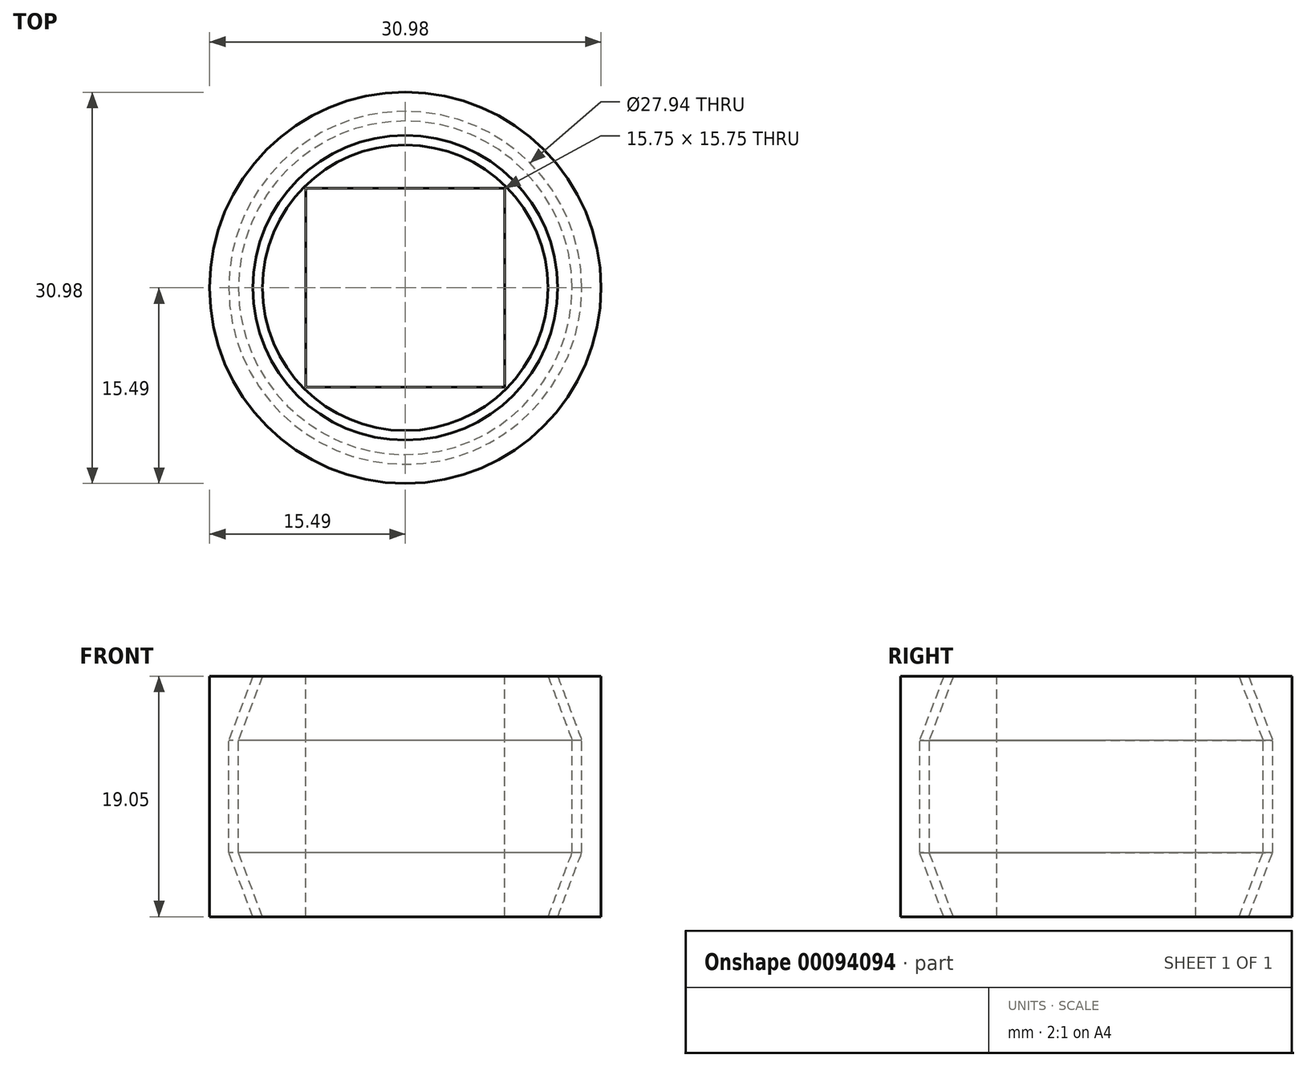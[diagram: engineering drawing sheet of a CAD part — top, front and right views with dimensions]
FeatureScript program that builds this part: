
annotation { "Feature Type Name" : "Feature", "Feature Type Description" : "" }
export const myFeature = defineFeature(function(context is Context, id is Id, definition is map)
    precondition{}
    {
        {
            var Q0;
            Q0=qCreatedBy(makeId("Front.planeOp"),FACE);
            var sketch = newSketch(context, id + "F0", { "sketchPlane" : qUnion([Q0])});
            skLineSegment(sketch, "E0", {"start": v(0, 52.04) * mm, "end": v(0, -73.81) * mm, "construction": true});
            skLineSegment(sketch, "E1.bottom", {"start": v(0, 19.05) * mm, "end": v(13.2, 19.05) * mm});
            skLineSegment(sketch, "E1.top", {"start": v(0, 0) * mm, "end": v(13.2, 0) * mm});
            skLineSegment(sketch, "E1.left", {"start": v(0, 19.05) * mm, "end": v(0, 0) * mm});
            skLineSegment(sketch, "E1.right", {"start": v(13.2, 19.05) * mm, "end": v(13.2, 0) * mm});
            skSolve(sketch);
        }
        {
            var Q0;
            Q0=makeQuery(id+"F0.imprint","IMPRINT",FACE,{"disambiguationData":[TD([[makeQuery(id+"F0.imprint","IMPRINT",EDGE,{"derivedFrom":sQuery(id+"F0.wireOp",EDGE,"E1.bottom")}),-1.0]])]});
            var Q1;
            Q1=sQuery(id+"F0.wireOp",EDGE,"E0");
            revolve(context, id + "F1", {"entities" : qUnion([Q0]), "axis" : qUnion([Q1]), "revolveType" : RevolveType.FULL});
        }
        {
            var Q0;
            Q0=makeQuery(id+"F1.opRevolve","SWEPT_FACE",FACE,{"disambiguationData":[OSD([sQuery(id+"F0.wireOp",EDGE,"E1.bottom")])]});
            var sketch = newSketch(context, id + "F2", { "sketchPlane" : qUnion([Q0])});
            skLineSegment(sketch, "E2.bottom", {"start": v(-7.87, 7.87) * mm, "end": v(7.87, 7.87) * mm});
            skLineSegment(sketch, "E2.top", {"start": v(-7.87, -7.87) * mm, "end": v(7.87, -7.87) * mm});
            skLineSegment(sketch, "E2.left", {"start": v(-7.87, 7.87) * mm, "end": v(-7.87, -7.87) * mm});
            skLineSegment(sketch, "E2.right", {"start": v(7.87, 7.87) * mm, "end": v(7.87, -7.87) * mm});
            skLineSegment(sketch, "E3", {"start": v(-7.87, 0) * mm, "end": v(7.87, 0) * mm, "construction": true});
            skPoint(sketch, "E4", {"position": v(0, 0) * mm});
            skSolve(sketch);
        }
        {
            var Q0;
            {var subQ0=sQuery(id+"F2.wireOp",EDGE,"E2.left");var subQ1=sQuery(id+"F2.wireOp",EDGE,"E2.bottom");var subQ2=makeQuery(id+"F2.imprint","INTERSECT",VERTEX,{"derivedFrom":[subQ1,subQ0]});Q0=makeQuery(id+"F2.imprint","IMPRINT",FACE,{"disambiguationData":[TD([[makeQuery(id+"F2.imprint","IMPRINT",EDGE,{"disambiguationData":[TD([[subQ2,-1.0]])],"derivedFrom":subQ1}),-1.0]])]});}
            var Q1;
            {var subQ0=sQuery(id+"F2.wireOp",EDGE,"E2.right");var subQ1=sQuery(id+"F2.wireOp",EDGE,"E2.bottom");var subQ2=makeQuery(id+"F2.imprint","INTERSECT",VERTEX,{"derivedFrom":[subQ1,subQ0]});Q1=makeQuery(id+"F2.imprint","IMPRINT",FACE,{"disambiguationData":[TD([[makeQuery(id+"F2.imprint","IMPRINT",EDGE,{"disambiguationData":[TD([[subQ2,1.0]])],"derivedFrom":subQ1}),-1.0]])]});}
            var Q2;
            {var subQ0=sQuery(id+"F2.wireOp",EDGE,"E2.left");var subQ1=sQuery(id+"F2.wireOp",EDGE,"E2.top");var subQ2=makeQuery(id+"F2.imprint","INTERSECT",VERTEX,{"derivedFrom":[subQ1,subQ0]});Q2=makeQuery(id+"F2.imprint","IMPRINT",FACE,{"disambiguationData":[TD([[makeQuery(id+"F2.imprint","IMPRINT",EDGE,{"disambiguationData":[TD([[subQ2,-1.0]])],"derivedFrom":subQ1}),1.0]])]});}
            var Q3;
            {var subQ0=sQuery(id+"F2.wireOp",EDGE,"E2.right");var subQ1=sQuery(id+"F2.wireOp",EDGE,"E2.top");var subQ2=makeQuery(id+"F2.imprint","INTERSECT",VERTEX,{"derivedFrom":[subQ1,subQ0]});Q3=makeQuery(id+"F2.imprint","IMPRINT",FACE,{"disambiguationData":[TD([[makeQuery(id+"F2.imprint","IMPRINT",EDGE,{"disambiguationData":[TD([[subQ2,1.0]])],"derivedFrom":subQ1}),1.0]])]});}
            extrude(context, id + "F3", {"entities" : qUnion([Q0, Q1, Q2, Q3]), "operationType" : NewBodyOperationType.REMOVE, "endBound" : BoundingType.THROUGH_ALL, "oppositeDirection" : true, "depth" : 25.4 * mm, "offsetDistance" : 25.4 * mm});
        }
        {
            var Q0;
            Q0=makeQuery(id+"F1.opRevolve","SWEPT_EDGE",EDGE,{"disambiguationData":[OSD([sQuery(id+"F0.wireOp",EDGE,"E1.bottom"),sQuery(id+"F0.wireOp",EDGE,"E1.right")])]});
            var Q1;
            Q1=makeQuery(id+"F1.opRevolve","SWEPT_EDGE",EDGE,{"disambiguationData":[OSD([sQuery(id+"F0.wireOp",EDGE,"E1.top"),sQuery(id+"F0.wireOp",EDGE,"E1.right")])]});
            chamfer(context, id + "F4", {"entities" : qUnion([Q0, Q1]), "chamferType" : ChamferType.TWO_OFFSETS, "width1" : 1.9 * mm, "oppositeDirection" : false, "width2" : 5.08 * mm, "tangentPropagation" : true});
        }
        {
            var Q0;
            Q0=qCreatedBy(makeId("Front.planeOp"),FACE);
            var sketch = newSketch(context, id + "F5", { "sketchPlane" : qUnion([Q0])});
            skLineSegment(sketch, "E5", {"start": v(11.3, 19.05) * mm, "end": v(13.2, 13.97) * mm});
            skLineSegment(sketch, "E6", {"start": v(13.2, 13.97) * mm, "end": v(13.2, 5.08) * mm});
            skLineSegment(sketch, "E7", {"start": v(13.2, 5.08) * mm, "end": v(11.3, 0) * mm});
            skLineSegment(sketch, "E8", {"start": v(11.3, 19.05) * mm, "end": v(12.07, 19.05) * mm});
            skLineSegment(sketch, "E9", {"start": v(12.07, 19.05) * mm, "end": v(13.97, 13.97) * mm});
            skLineSegment(sketch, "E10", {"start": v(13.97, 13.97) * mm, "end": v(13.97, 5.08) * mm});
            skLineSegment(sketch, "E11", {"start": v(13.97, 5.08) * mm, "end": v(12.07, 0) * mm});
            skLineSegment(sketch, "E12", {"start": v(11.3, 0) * mm, "end": v(12.07, 0) * mm});
            skLineSegment(sketch, "E13", {"start": v(13.2, 13.97) * mm, "end": v(13.97, 13.97) * mm, "construction": true});
            skLineSegment(sketch, "E14.0", {"start": v(-11.3, 19.05) * mm, "end": v(11.3, 19.05) * mm});
            skLineSegment(sketch, "E15", {"start": v(12.07, 0) * mm, "end": v(15.5, 0) * mm});
            skLineSegment(sketch, "E16", {"start": v(15.5, 0) * mm, "end": v(15.5, 19.05) * mm});
            skLineSegment(sketch, "E17", {"start": v(15.5, 19.05) * mm, "end": v(12.07, 19.05) * mm});
            skLineSegment(sketch, "E18.0", {"start": v(0, 0) * mm, "end": v(13.2, 0) * mm});
            skSolve(sketch);
        }
        {
            var Q0;
            Q0=makeQuery(id+"F5.imprint","IMPRINT",FACE,{"disambiguationData":[TD([[makeQuery(id+"F5.imprint","IMPRINT",EDGE,{"derivedFrom":sQuery(id+"F5.wireOp",EDGE,"E9")}),1.0]])]});
            var Q1;
            Q1=sQuery(id+"F0.wireOp",EDGE,"E0");
            revolve(context, id + "F6", {"entities" : qUnion([Q0]), "axis" : qUnion([Q1]), "revolveType" : RevolveType.FULL});
        }
    });
